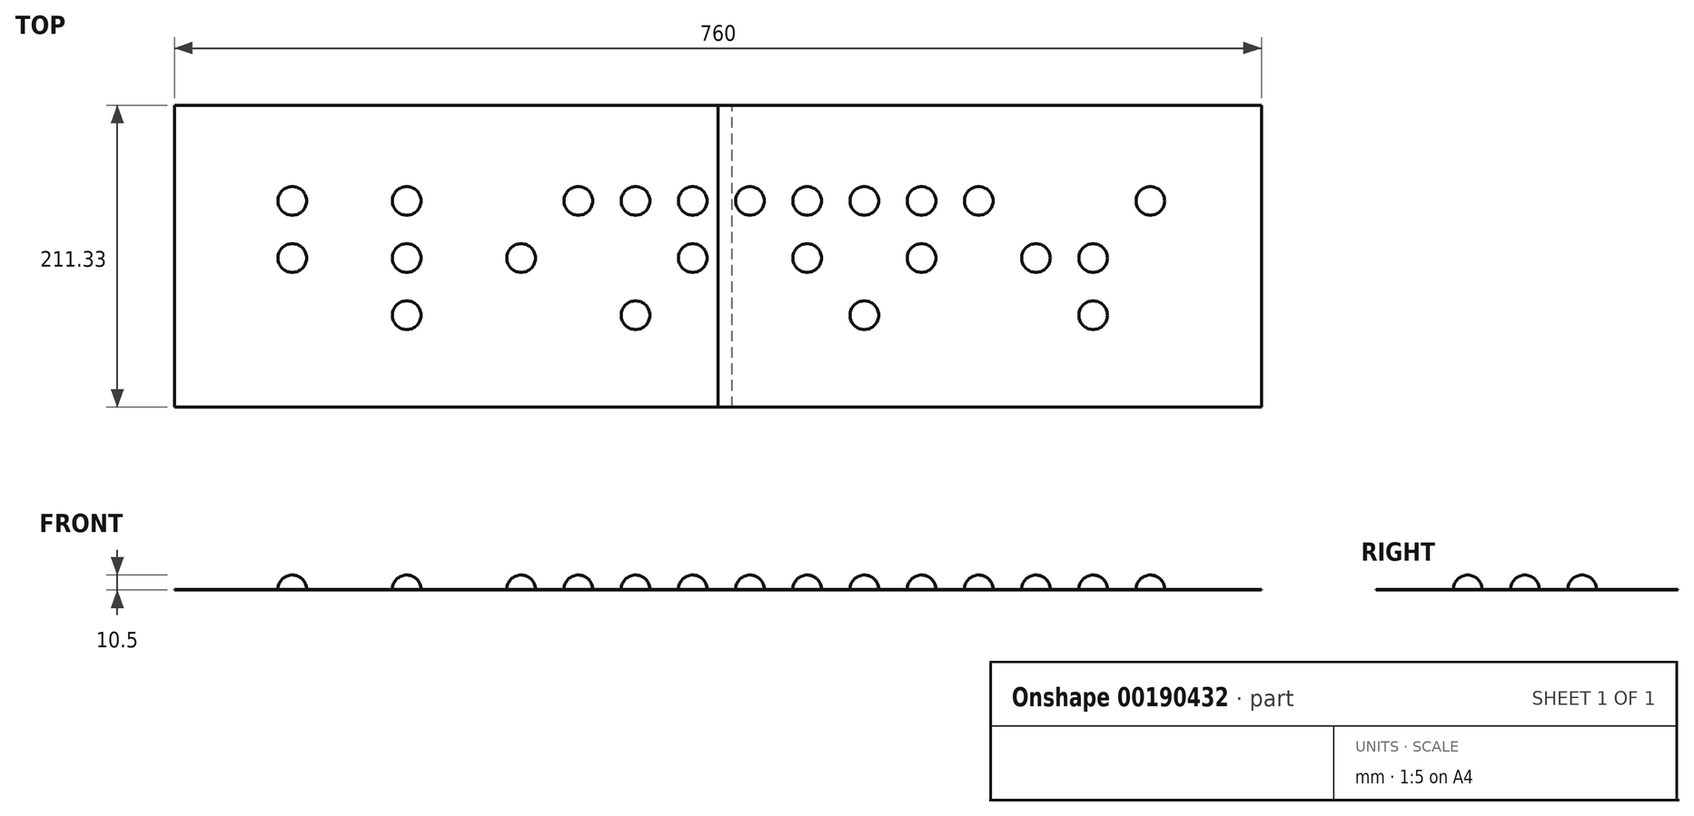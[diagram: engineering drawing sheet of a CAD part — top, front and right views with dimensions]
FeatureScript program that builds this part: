
annotation { "Feature Type Name" : "Feature", "Feature Type Description" : "" }
export const myFeature = defineFeature(function(context is Context, id is Id, definition is map)
    precondition{}
    {
        {
            var Q0;
            Q0=qCreatedBy(makeId("Top.planeOp"),FACE);
            var sketch = newSketch(context, id + "F0", { "sketchPlane" : qUnion([Q0])});
            skSolve(sketch);
        }
        {
            var Q0;
            Q0=qCreatedBy(makeId("Top.planeOp"),FACE);
            var sketch = newSketch(context, id + "F1", { "sketchPlane" : qUnion([Q0])});
            skLineSegment(sketch, "E0.bottom", {"start": v(-380, 107.06) * mm, "end": v(0, 107.06) * mm});
            skLineSegment(sketch, "E0.top", {"start": v(-380, -104.27) * mm, "end": v(0, -104.27) * mm});
            skLineSegment(sketch, "E0.left", {"start": v(-380, 107.06) * mm, "end": v(-380, -104.27) * mm});
            skLineSegment(sketch, "E0.right", {"start": v(0, 107.06) * mm, "end": v(0, -104.27) * mm});
            skSolve(sketch);
        }
        {
            var Q0;
            Q0 = qSketchRegion(id + "F1", true);
            extrude(context, id + "F2", {"entities" : qUnion([Q0]), "depth" : 0.5 * mm});
        }
        {
            var Q0;
            Q0=makeQuery(id+"F2.opExtrude","CAP_FACE",FACE,{"disambiguationData":[OSD([sQuery(id+"F1.wireOp",EDGE,"E0.bottom"),sQuery(id+"F1.wireOp",EDGE,"E0.top"),sQuery(id+"F1.wireOp",EDGE,"E0.left"),sQuery(id+"F1.wireOp",EDGE,"E0.right")])],"isStart":false});
            var sketch = newSketch(context, id + "F3", { "sketchPlane" : qUnion([Q0])});
            skCircle(sketch, "E1", {"center": v(-297.6, 40.06) * mm, "radius": 10 * mm});
            skCircle(sketch, "E2.0.1.0", {"center": v(-297.6, 0.06) * mm, "radius": 10 * mm});
            skCircle(sketch, "E2.2.0.0", {"center": v(-217.6, 40.06) * mm, "radius": 10 * mm});
            skCircle(sketch, "E2.2.1.0", {"center": v(-217.6, 0.06) * mm, "radius": 10 * mm});
            skCircle(sketch, "E2.2.2.0", {"center": v(-217.6, -39.94) * mm, "radius": 10 * mm});
            skCircle(sketch, "E2.4.1.0", {"center": v(-137.6, 0.06) * mm, "radius": 10 * mm});
            skCircle(sketch, "E2.5.0.0", {"center": v(-97.6, 40.06) * mm, "radius": 10 * mm});
            skCircle(sketch, "E2.6.0.0", {"center": v(-57.6, 40.06) * mm, "radius": 10 * mm});
            skCircle(sketch, "E2.6.2.0", {"center": v(-57.6, -39.94) * mm, "radius": 10 * mm});
            skCircle(sketch, "E2.7.0.0", {"center": v(-17.6, 40.06) * mm, "radius": 10 * mm});
            skCircle(sketch, "E2.7.1.0", {"center": v(-17.6, 0.06) * mm, "radius": 10 * mm});
            skLineSegment(sketch, "E2.direction1", {"start": v(-297.6, 40.06) * mm, "end": v(-257.6, 40.06) * mm, "construction": true});
            skLineSegment(sketch, "E2.direction2", {"start": v(-297.6, 40.06) * mm, "end": v(-297.6, 0.06) * mm, "construction": true});
            skSolve(sketch);
        }
        {
            var Q0;
            Q0 = qSketchRegion(id + "F3", true);
            extrude(context, id + "F4", {"entities" : qUnion([Q0]), "operationType" : NewBodyOperationType.ADD, "depth" : 10 * mm});
        }
        {
            var Q0;
            Q0=makeQuery(id+"F4.opExtrude","CAP_EDGE",EDGE,{"disambiguationData":[OSD([sQuery(id+"F3.wireOp",EDGE,"E1")])],"isStart":false});
            var Q1;
            Q1=makeQuery(id+"F4.opExtrude","CAP_EDGE",EDGE,{"disambiguationData":[OSD([sQuery(id+"F3.wireOp",EDGE,"E2.0.1.0")])],"isStart":false});
            var Q2;
            Q2=makeQuery(id+"F4.opExtrude","CAP_EDGE",EDGE,{"disambiguationData":[OSD([sQuery(id+"F3.wireOp",EDGE,"E2.2.0.0")])],"isStart":false});
            var Q3;
            Q3=makeQuery(id+"F4.opExtrude","CAP_EDGE",EDGE,{"disambiguationData":[OSD([sQuery(id+"F3.wireOp",EDGE,"E2.2.1.0")])],"isStart":false});
            var Q4;
            Q4=makeQuery(id+"F4.opExtrude","CAP_EDGE",EDGE,{"disambiguationData":[OSD([sQuery(id+"F3.wireOp",EDGE,"E2.2.2.0")])],"isStart":false});
            var Q5;
            Q5=makeQuery(id+"F4.opExtrude","CAP_EDGE",EDGE,{"disambiguationData":[OSD([sQuery(id+"F3.wireOp",EDGE,"E2.4.1.0")])],"isStart":false});
            var Q6;
            Q6=makeQuery(id+"F4.opExtrude","CAP_EDGE",EDGE,{"disambiguationData":[OSD([sQuery(id+"F3.wireOp",EDGE,"E2.5.0.0")])],"isStart":false});
            var Q7;
            Q7=makeQuery(id+"F4.opExtrude","CAP_EDGE",EDGE,{"disambiguationData":[OSD([sQuery(id+"F3.wireOp",EDGE,"E2.6.0.0")])],"isStart":false});
            var Q8;
            Q8=makeQuery(id+"F4.opExtrude","CAP_EDGE",EDGE,{"disambiguationData":[OSD([sQuery(id+"F3.wireOp",EDGE,"E2.7.0.0")])],"isStart":false});
            var Q9;
            Q9=makeQuery(id+"F4.opExtrude","CAP_FACE",FACE,{"disambiguationData":[OSD([sQuery(id+"F3.wireOp",EDGE,"E2.7.1.0")])],"isStart":false});
            var Q10;
            Q10=makeQuery(id+"F4.opExtrude","CAP_EDGE",EDGE,{"disambiguationData":[OSD([sQuery(id+"F3.wireOp",EDGE,"E2.6.2.0")])],"isStart":false});
            fillet(context, id + "F5", {"entities" : qUnion([Q0, Q1, Q2, Q3, Q4, Q5, Q6, Q7, Q8, Q9, Q10]), "radius" : 10 * mm, "tangentPropagation" : true, "allowEdgeOverflow" : false});
        }
        {
            var Q0;
            Q0=makeQuery(id+"F2.opExtrude","CAP_FACE",FACE,{"disambiguationData":[OSD([sQuery(id+"F1.wireOp",EDGE,"E0.bottom"),sQuery(id+"F1.wireOp",EDGE,"E0.top"),sQuery(id+"F1.wireOp",EDGE,"E0.left"),sQuery(id+"F1.wireOp",EDGE,"E0.right")])],"isStart":true});
            var sketch = newSketch(context, id + "F6", { "sketchPlane" : qUnion([Q0])});
            skLineSegment(sketch, "E3.bottom", {"start": v(0, 104.27) * mm, "end": v(10, 104.27) * mm});
            skLineSegment(sketch, "E3.top", {"start": v(0, -107.06) * mm, "end": v(10, -107.06) * mm});
            skLineSegment(sketch, "E3.left", {"start": v(0, 104.27) * mm, "end": v(0, -107.06) * mm});
            skLineSegment(sketch, "E3.right", {"start": v(10, 104.27) * mm, "end": v(10, -107.06) * mm});
            skSolve(sketch);
        }
        {
            var Q0;
            Q0 = qSketchRegion(id + "F6", true);
            extrude(context, id + "F7", {"entities" : qUnion([Q0]), "operationType" : NewBodyOperationType.ADD, "oppositeDirection" : true, "depth" : 0.3 * mm});
        }
        {
            var Q0;
            Q0=qCreatedBy(makeId("Top.planeOp"),FACE);
            var sketch = newSketch(context, id + "F8", { "sketchPlane" : qUnion([Q0])});
            skLineSegment(sketch, "E4.bottom", {"start": v(0, 107.06) * mm, "end": v(380, 107.06) * mm});
            skLineSegment(sketch, "E4.top", {"start": v(0, -104.27) * mm, "end": v(380, -104.27) * mm});
            skLineSegment(sketch, "E4.left", {"start": v(0, 107.06) * mm, "end": v(0, -104.27) * mm});
            skLineSegment(sketch, "E4.right", {"start": v(380, 107.06) * mm, "end": v(380, -104.27) * mm});
            skSolve(sketch);
        }
        {
            var Q0;
            Q0 = qSketchRegion(id + "F8", true);
            extrude(context, id + "F9", {"entities" : qUnion([Q0]), "depth" : 0.5 * mm});
        }
        {
            var Q0;
            Q0=makeQuery(id+"F9.opExtrude","CAP_FACE",FACE,{"disambiguationData":[OSD([sQuery(id+"F8.wireOp",EDGE,"E4.bottom"),sQuery(id+"F8.wireOp",EDGE,"E4.top"),sQuery(id+"F8.wireOp",EDGE,"E4.left"),sQuery(id+"F8.wireOp",EDGE,"E4.right")])],"isStart":false});
            var sketch = newSketch(context, id + "F10", { "sketchPlane" : qUnion([Q0])});
            skCircle(sketch, "E5.1.0.0", {"center": v(22.4, 40.06) * mm, "radius": 10 * mm});
            skCircle(sketch, "E5.2.0.0", {"center": v(62.4, 40.06) * mm, "radius": 10 * mm});
            skCircle(sketch, "E5.2.1.0", {"center": v(62.4, 0.06) * mm, "radius": 10 * mm});
            skCircle(sketch, "E5.3.0.0", {"center": v(102.4, 40.06) * mm, "radius": 10 * mm});
            skCircle(sketch, "E5.3.2.0", {"center": v(102.4, -39.94) * mm, "radius": 10 * mm});
            skCircle(sketch, "E5.4.0.0", {"center": v(142.4, 40.06) * mm, "radius": 10 * mm});
            skCircle(sketch, "E5.4.1.0", {"center": v(142.4, 0.06) * mm, "radius": 10 * mm});
            skCircle(sketch, "E5.5.0.0", {"center": v(182.4, 40.06) * mm, "radius": 10 * mm});
            skCircle(sketch, "E5.6.1.0", {"center": v(222.4, 0.06) * mm, "radius": 10 * mm});
            skCircle(sketch, "E5.7.1.0", {"center": v(262.4, 0.06) * mm, "radius": 10 * mm});
            skCircle(sketch, "E5.7.2.0", {"center": v(262.4, -39.94) * mm, "radius": 10 * mm});
            skCircle(sketch, "E5.8.0.0", {"center": v(302.4, 40.06) * mm, "radius": 10 * mm});
            skLineSegment(sketch, "E5.direction1", {"start": v(-17.6, 40.06) * mm, "end": v(22.4, 40.06) * mm, "construction": true});
            skLineSegment(sketch, "E5.direction2", {"start": v(-17.6, 40.06) * mm, "end": v(-17.6, 0.06) * mm, "construction": true});
            skSolve(sketch);
        }
        {
            var Q0;
            Q0 = qSketchRegion(id + "F10", true);
            extrude(context, id + "F11", {"entities" : qUnion([Q0]), "operationType" : NewBodyOperationType.ADD, "depth" : 10 * mm});
        }
        {
            var Q0;
            Q0=makeQuery(id+"F11.opExtrude","CAP_FACE",FACE,{"disambiguationData":[OSD([sQuery(id+"F10.wireOp",EDGE,"E5.1.0.0")])],"isStart":false});
            var Q1;
            Q1=makeQuery(id+"F11.opExtrude","CAP_EDGE",EDGE,{"disambiguationData":[OSD([sQuery(id+"F10.wireOp",EDGE,"E5.2.0.0")])],"isStart":false});
            var Q2;
            Q2=makeQuery(id+"F11.opExtrude","CAP_EDGE",EDGE,{"disambiguationData":[OSD([sQuery(id+"F10.wireOp",EDGE,"E5.3.0.0")])],"isStart":false});
            var Q3;
            Q3=makeQuery(id+"F11.opExtrude","CAP_EDGE",EDGE,{"disambiguationData":[OSD([sQuery(id+"F10.wireOp",EDGE,"E5.4.0.0")])],"isStart":false});
            var Q4;
            Q4=makeQuery(id+"F11.opExtrude","CAP_FACE",FACE,{"disambiguationData":[OSD([sQuery(id+"F10.wireOp",EDGE,"E5.5.0.0")])],"isStart":false});
            var Q5;
            Q5=makeQuery(id+"F11.opExtrude","CAP_EDGE",EDGE,{"disambiguationData":[OSD([sQuery(id+"F10.wireOp",EDGE,"E5.6.1.0")])],"isStart":false});
            var Q6;
            Q6=makeQuery(id+"F11.opExtrude","CAP_EDGE",EDGE,{"disambiguationData":[OSD([sQuery(id+"F10.wireOp",EDGE,"E5.7.1.0")])],"isStart":false});
            var Q7;
            Q7=makeQuery(id+"F11.opExtrude","CAP_EDGE",EDGE,{"disambiguationData":[OSD([sQuery(id+"F10.wireOp",EDGE,"E5.8.0.0")])],"isStart":false});
            var Q8;
            Q8=makeQuery(id+"F11.opExtrude","CAP_EDGE",EDGE,{"disambiguationData":[OSD([sQuery(id+"F10.wireOp",EDGE,"E5.7.2.0")])],"isStart":false});
            var Q9;
            Q9=makeQuery(id+"F11.opExtrude","CAP_EDGE",EDGE,{"disambiguationData":[OSD([sQuery(id+"F10.wireOp",EDGE,"E5.4.1.0")])],"isStart":false});
            var Q10;
            Q10=makeQuery(id+"F11.opExtrude","CAP_EDGE",EDGE,{"disambiguationData":[OSD([sQuery(id+"F10.wireOp",EDGE,"E5.3.2.0")])],"isStart":false});
            var Q11;
            Q11=makeQuery(id+"F11.opExtrude","CAP_EDGE",EDGE,{"disambiguationData":[OSD([sQuery(id+"F10.wireOp",EDGE,"E5.2.1.0")])],"isStart":false});
            fillet(context, id + "F12", {"entities" : qUnion([Q0, Q1, Q2, Q3, Q4, Q5, Q6, Q7, Q8, Q9, Q10, Q11]), "radius" : 10 * mm, "tangentPropagation" : true, "allowEdgeOverflow" : false});
        }
    });
